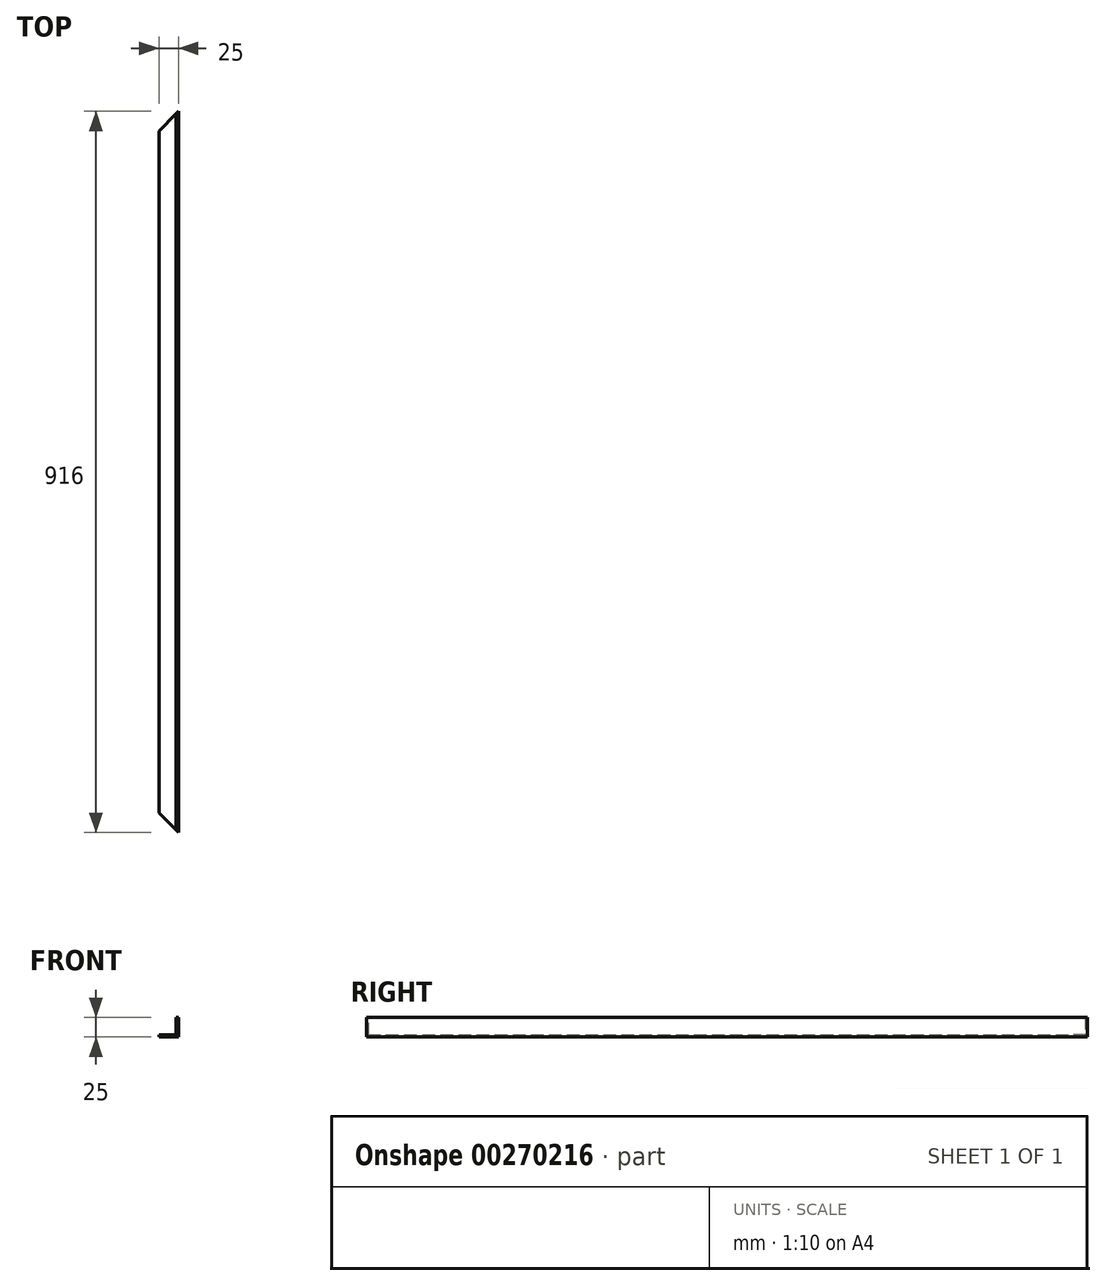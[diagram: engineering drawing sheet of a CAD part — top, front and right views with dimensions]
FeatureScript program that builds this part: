
annotation { "Feature Type Name" : "Feature", "Feature Type Description" : "" }
export const myFeature = defineFeature(function(context is Context, id is Id, definition is map)
    precondition{}
    {
        {
            var Q0;
            Q0=qCreatedBy(makeId("Front.planeOp"),FACE);
            var sketch = newSketch(context, id + "F0", { "sketchPlane" : qUnion([Q0])});
            skLineSegment(sketch, "E0", {"start": v(0, 0) * mm, "end": v(25, 0) * mm});
            skLineSegment(sketch, "E1", {"start": v(25, 0) * mm, "end": v(25, 25) * mm});
            skLineSegment(sketch, "E2", {"start": v(25, 25) * mm, "end": v(22, 25) * mm});
            skLineSegment(sketch, "E3", {"start": v(22, 25) * mm, "end": v(22, 3) * mm});
            skLineSegment(sketch, "E4", {"start": v(22, 3) * mm, "end": v(0, 3) * mm});
            skLineSegment(sketch, "E5", {"start": v(0, 3) * mm, "end": v(0, 0) * mm});
            skSolve(sketch);
        }
        {
            var Q0;
            Q0=makeQuery(id+"F0.imprint","IMPRINT",FACE,{"disambiguationData":[TD([[makeQuery(id+"F0.imprint","IMPRINT",EDGE,{"derivedFrom":sQuery(id+"F0.wireOp",EDGE,"E0")}),1.0]])]});
            extrude(context, id + "F1", {"entities" : qUnion([Q0]), "depth" : 920 * mm});
        }
        {
            var Q0;
            Q0=makeQuery(id+"F1.opExtrude","CAP_EDGE",EDGE,{"disambiguationData":[OSD([sQuery(id+"F0.wireOp",EDGE,"E3")])],"isStart":true});
            chamfer(context, id + "F2", {"entities" : qUnion([Q0]), "width" : 5 * mm, "tangentPropagation" : true});
        }
        {
            var Q0;
            Q0=makeQuery(id+"F1.opExtrude","SWEPT_FACE",FACE,{"disambiguationData":[OSD([sQuery(id+"F0.wireOp",EDGE,"E4")])]});
            var sketch = newSketch(context, id + "F3", { "sketchPlane" : qUnion([Q0])});
            skLineSegment(sketch, "E6", {"start": v(25, -2) * mm, "end": v(0, -27) * mm});
            skSolve(sketch);
        }
        {
            var Q0;
            {var subQ0=sQuery(id+"F0.wireOp",EDGE,"E4");var subQ7=makeQuery(id+"F1.opExtrude","CAP_EDGE",EDGE,{"disambiguationData":[OSD([subQ0])],"isStart":true});Q0=makeQuery(id+"F3.imprint","IMPRINT",FACE,{"disambiguationData":[TD([[makeQuery(id+"F3.imprint","IMPRINT",EDGE,{"derivedFrom":subQ7}),1.0]])]});}
            extrude(context, id + "F4", {"entities" : qUnion([Q0]), "operationType" : NewBodyOperationType.REMOVE, "oppositeDirection" : true, "depth" : 25 * mm});
        }
        {
            var Q0;
            Q0=makeQuery(id+"F1.opExtrude","CAP_EDGE",EDGE,{"disambiguationData":[OSD([sQuery(id+"F0.wireOp",EDGE,"E3")])],"isStart":false});
            chamfer(context, id + "F5", {"entities" : qUnion([Q0]), "width" : 5 * mm, "tangentPropagation" : true});
        }
        {
            var Q0;
            Q0=makeQuery(id+"F1.opExtrude","SWEPT_FACE",FACE,{"disambiguationData":[OSD([sQuery(id+"F0.wireOp",EDGE,"E4")])]});
            var sketch = newSketch(context, id + "F6", { "sketchPlane" : qUnion([Q0])});
            skLineSegment(sketch, "E7", {"start": v(25, -918) * mm, "end": v(0, -893) * mm});
            skSolve(sketch);
        }
        {
            var Q0;
            {var subQ0=sQuery(id+"F0.wireOp",EDGE,"E4");var subQ5=makeQuery(id+"F1.opExtrude","CAP_EDGE",EDGE,{"disambiguationData":[OSD([subQ0])],"isStart":false});Q0=makeQuery(id+"F6.imprint","IMPRINT",FACE,{"disambiguationData":[TD([[makeQuery(id+"F6.imprint","IMPRINT",EDGE,{"derivedFrom":subQ5}),-1.0]])]});}
            extrude(context, id + "F7", {"entities" : qUnion([Q0]), "operationType" : NewBodyOperationType.REMOVE, "oppositeDirection" : true, "depth" : 25 * mm});
        }
    });
